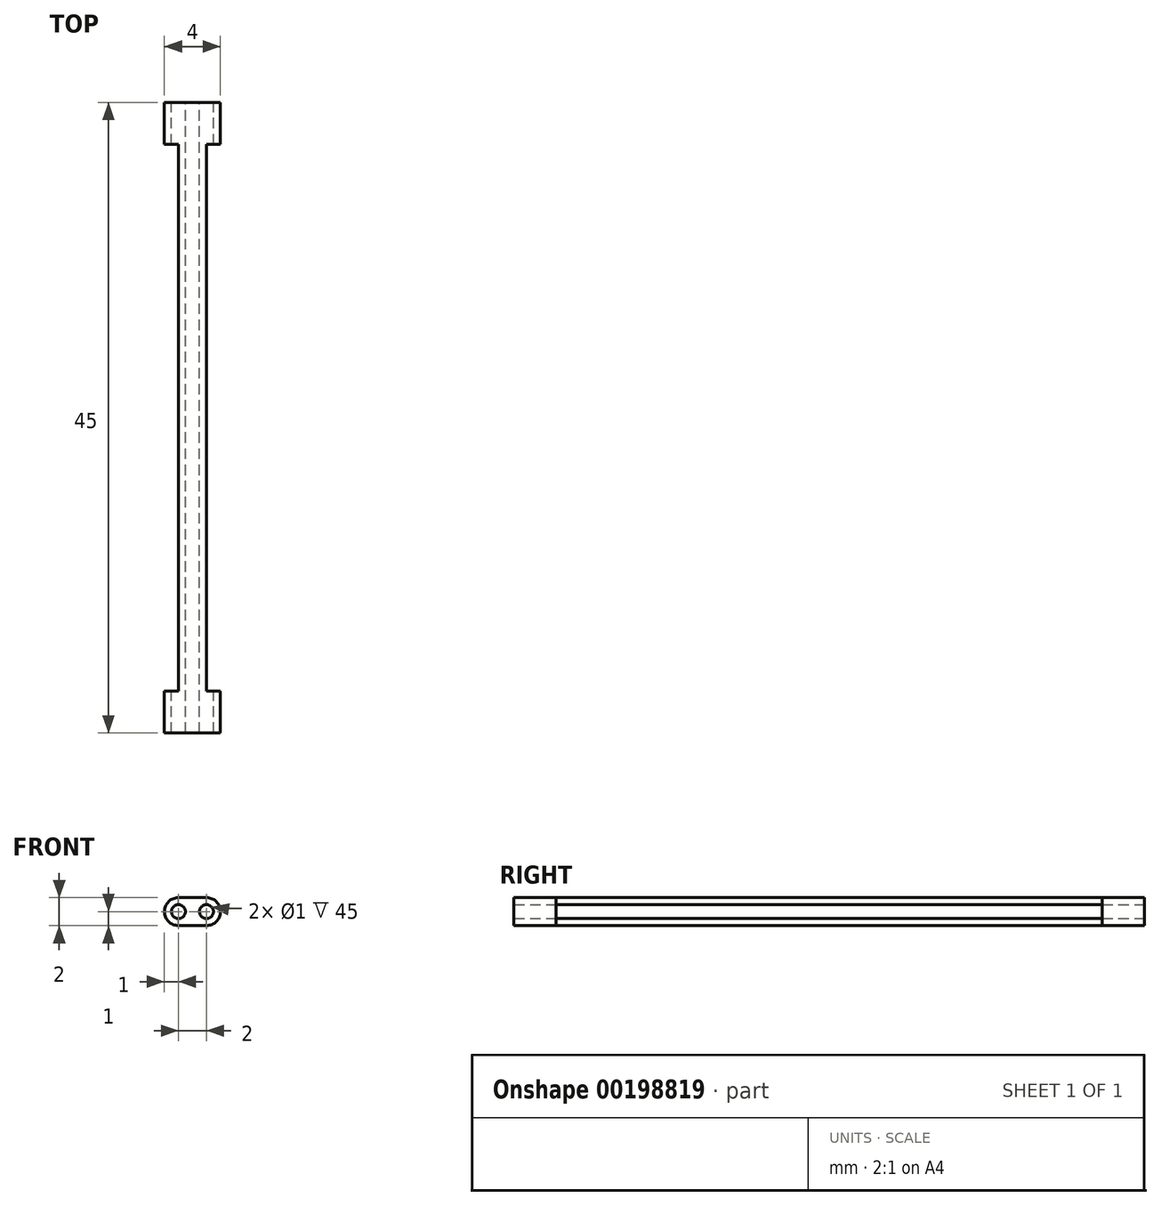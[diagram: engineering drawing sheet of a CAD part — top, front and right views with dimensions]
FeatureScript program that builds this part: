
annotation { "Feature Type Name" : "Feature", "Feature Type Description" : "" }
export const myFeature = defineFeature(function(context is Context, id is Id, definition is map)
    precondition{}
    {
        {
            var Q0;
            Q0=qCreatedBy(makeId("Front.planeOp"),FACE);
            var sketch = newSketch(context, id + "F0", { "sketchPlane" : qUnion([Q0])});
            skLineSegment(sketch, "E0", {"start": v(0, 0) * mm, "end": v(1, 0) * mm, "construction": true});
            skCircle(sketch, "E1", {"center": v(1, 0) * mm, "radius": 0.5 * mm});
            skLineSegment(sketch, "E2", {"start": v(0, 0) * mm, "end": v(0, 1.9) * mm, "construction": true});
            skArc(sketch, "E3.MirrorC", {"start": v(-1, -1) * mm, "mid": v(-2, 0) * mm, "end": v(-1, 1) * mm});
            skCircle(sketch, "E4.MirrorC", {"center": v(-1, 0) * mm, "radius": 0.5 * mm});
            skLineSegment(sketch, "E5", {"start": v(-1, 1) * mm, "end": v(1, 1) * mm});
            skLineSegment(sketch, "E6.0", {"start": v(-1, -1) * mm, "end": v(1, -1) * mm});
            skArc(sketch, "E7", {"start": v(1, -1) * mm, "mid": v(2, 0) * mm, "end": v(1, 1) * mm});
            skSolve(sketch);
        }
        {
            var Q0;
            Q0=makeQuery(id+"F0.imprint","IMPRINT",FACE,{"disambiguationData":[TD([[makeQuery(id+"F0.imprint","IMPRINT",EDGE,{"derivedFrom":sQuery(id+"F0.wireOp",EDGE,"E1")}),-1.0]])]});
            extrude(context, id + "F1", {"entities" : qUnion([Q0]), "endBound" : BoundingType.SYMMETRIC, "depth" : 45 * mm});
        }
        {
            var Q0;
            Q0=makeQuery(id+"F1.opExtrude","SWEPT_FACE",FACE,{"disambiguationData":[OSD([sQuery(id+"F0.wireOp",EDGE,"E5")])]});
            var sketch = newSketch(context, id + "F2", { "sketchPlane" : qUnion([Q0])});
            skLineSegment(sketch, "E8.bottom", {"start": v(0.5, -19.5) * mm, "end": v(-0.5, -19.5) * mm});
            skLineSegment(sketch, "E8.top", {"start": v(0.5, 19.5) * mm, "end": v(-0.5, 19.5) * mm});
            skLineSegment(sketch, "E8.left", {"start": v(0.5, -19.5) * mm, "end": v(0.5, 19.5) * mm});
            skLineSegment(sketch, "E8.right", {"start": v(-0.5, -19.5) * mm, "end": v(-0.5, 19.5) * mm});
            skPoint(sketch, "E8.middle", {"position": v(0, 0) * mm});
            skLineSegment(sketch, "E9.bottom", {"start": v(0.5, 19.5) * mm, "end": v(2, 19.5) * mm});
            skLineSegment(sketch, "E9.top", {"start": v(0.5, -19.5) * mm, "end": v(2, -19.5) * mm});
            skLineSegment(sketch, "E9.left", {"start": v(0.5, 19.5) * mm, "end": v(0.5, -19.5) * mm});
            skLineSegment(sketch, "E9.right", {"start": v(2, 19.5) * mm, "end": v(2, -19.5) * mm});
            skLineSegment(sketch, "E10.bottom", {"start": v(-0.5, 19.5) * mm, "end": v(-2, 19.5) * mm});
            skLineSegment(sketch, "E10.top", {"start": v(-0.5, -19.5) * mm, "end": v(-2, -19.5) * mm});
            skLineSegment(sketch, "E10.left", {"start": v(-0.5, 19.5) * mm, "end": v(-0.5, -19.5) * mm});
            skLineSegment(sketch, "E10.right", {"start": v(-2, 19.5) * mm, "end": v(-2, -19.5) * mm});
            skSolve(sketch);
        }
        {
            var Q0;
            {var subQ0=sQuery(id+"F2.wireOp",EDGE,"E9.right");Q0=makeQuery(id+"F2.imprint","IMPRINT",FACE,{"disambiguationData":[TD([[makeQuery(id+"F2.imprint","IMPRINT",EDGE,{"derivedFrom":subQ0}),-1.0]])]});}
            var Q1;
            {var subQ0=sQuery(id+"F2.wireOp",EDGE,"E9.left");Q1=makeQuery(id+"F2.imprint","IMPRINT",FACE,{"disambiguationData":[TD([[makeQuery(id+"F2.imprint","IMPRINT",EDGE,{"derivedFrom":subQ0}),1.0]])]});}
            var Q2;
            {var subQ0=sQuery(id+"F2.wireOp",EDGE,"E10.right");Q2=makeQuery(id+"F2.imprint","IMPRINT",FACE,{"disambiguationData":[TD([[makeQuery(id+"F2.imprint","IMPRINT",EDGE,{"derivedFrom":subQ0}),1.0]])]});}
            var Q3;
            {var subQ0=sQuery(id+"F2.wireOp",EDGE,"E10.left");Q3=makeQuery(id+"F2.imprint","IMPRINT",FACE,{"disambiguationData":[TD([[makeQuery(id+"F2.imprint","IMPRINT",EDGE,{"derivedFrom":subQ0}),-1.0]])]});}
            extrude(context, id + "F3", {"entities" : qUnion([Q0, Q1, Q2, Q3]), "operationType" : NewBodyOperationType.REMOVE, "oppositeDirection" : true, "depth" : 25 * mm});
        }
    });
